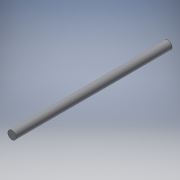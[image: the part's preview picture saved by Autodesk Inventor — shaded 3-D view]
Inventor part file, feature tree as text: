
AUTODESK INVENTOR PART (.ipt)
format: ipt  version: 2019 (Build 230136000, 136)  size: 91,136 bytes
history: native  units: mm
features: extrude x1, sketch x1
ambient origin geometry x8: Origin, YZ Plane, XZ Plane, XY Plane, X Axis, Y Axis, Z Axis, Center Point
bodies: Solid1 (feature_tree)
feature tree (2):
  extrude  "Extrusion1"  Depth=300.0mm TaperAngle=0.0deg
  sketch  "Sketch1"  dims[d0=16.0mm d1=300.0mm d2=0.0mm]
